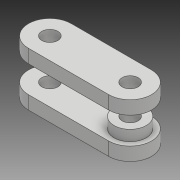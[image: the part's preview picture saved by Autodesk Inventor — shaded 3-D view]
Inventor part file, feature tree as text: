
AUTODESK INVENTOR PART (.ipt)
format: ipt  version: 2018 (Build 220112000, 112)  size: 236,032 bytes
history: native  units: mm
features: extrude x4, sketch x4, other x1, projected_geometry x1
ambient origin geometry x8: Origin, YZ Plane, XZ Plane, XY Plane, X Axis, Y Axis, Z Axis, Center Point
bodies: Body1 (feature_tree)
feature tree (10):
  other  "ソリッド1"
  extrude  "押し出し1"  Depth=4.0mm
  extrude  "押し出し2"  Depth=15.0mm
  extrude  "押し出し3"  Depth=10.0mm TaperAngle=0.0deg
  extrude  "押し出し4"  Depth=5.0mm TaperAngle=0.0deg
  sketch  "スケッチ1"
  sketch  "スケッチ2"
  projected_geometry  "投影ループ1"
  sketch  "スケッチ3"
  sketch  "スケッチ4"
